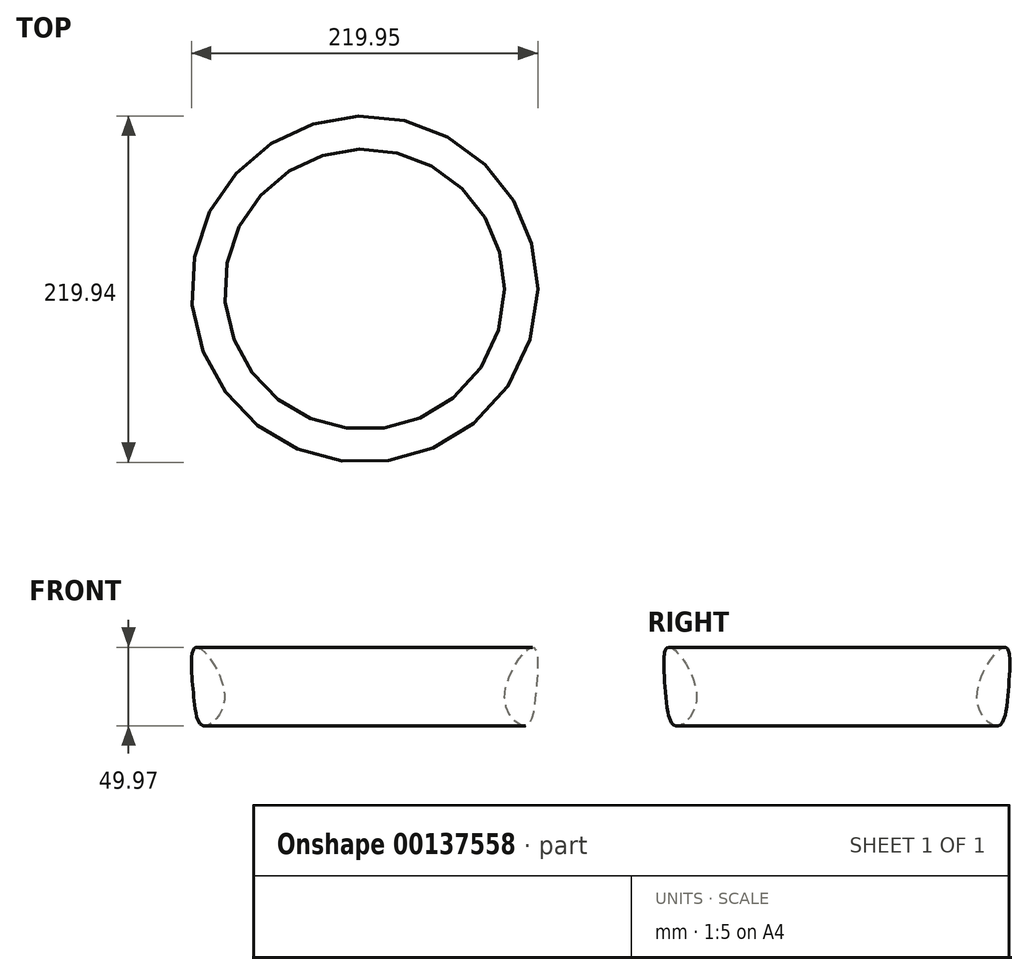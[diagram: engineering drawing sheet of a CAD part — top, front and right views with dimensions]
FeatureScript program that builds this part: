
annotation { "Feature Type Name" : "Feature", "Feature Type Description" : "" }
export const myFeature = defineFeature(function(context is Context, id is Id, definition is map)
    precondition{}
    {
        {
            var Q0;
            Q0=qCreatedBy(makeId("Top.planeOp"),FACE);
            var sketch = newSketch(context, id + "F0", { "sketchPlane" : qUnion([Q0])});
            skCircle(sketch, "E0", {"center": v(102.23, 0) * mm, "radius": 102.23 * mm});
            skSolve(sketch);
        }
        {
            var Q0;
            Q0=qCreatedBy(makeId("Front.planeOp"),FACE);
            var sketch = newSketch(context, id + "F1", { "sketchPlane" : qUnion([Q0])});
            skFitSpline(sketch, "E1", {"points": [v(0, -30.57) * mm, v(-6.63, -8.3) * mm, v(-4.6, 19.34) * mm, v(13.27, -12.75) * mm, v(0, -30.57) * mm]});
            skSolve(sketch);
        }
        {
            var Q0;
            Q0=makeQuery(id+"F1.imprint","IMPRINT",FACE,{"disambiguationData":[TD([[makeQuery(id+"F1.imprint","IMPRINT",EDGE,{"derivedFrom":sQuery(id+"F1.wireOp",EDGE,"E1")}),-1.0]])]});
            var Q1;
            Q1=sQuery(id+"F0.wireOp",EDGE,"E0");
            sweep(context, id + "F2", {"profiles" : qUnion([Q0]), "path" : qUnion([Q1])});
        }
    });
